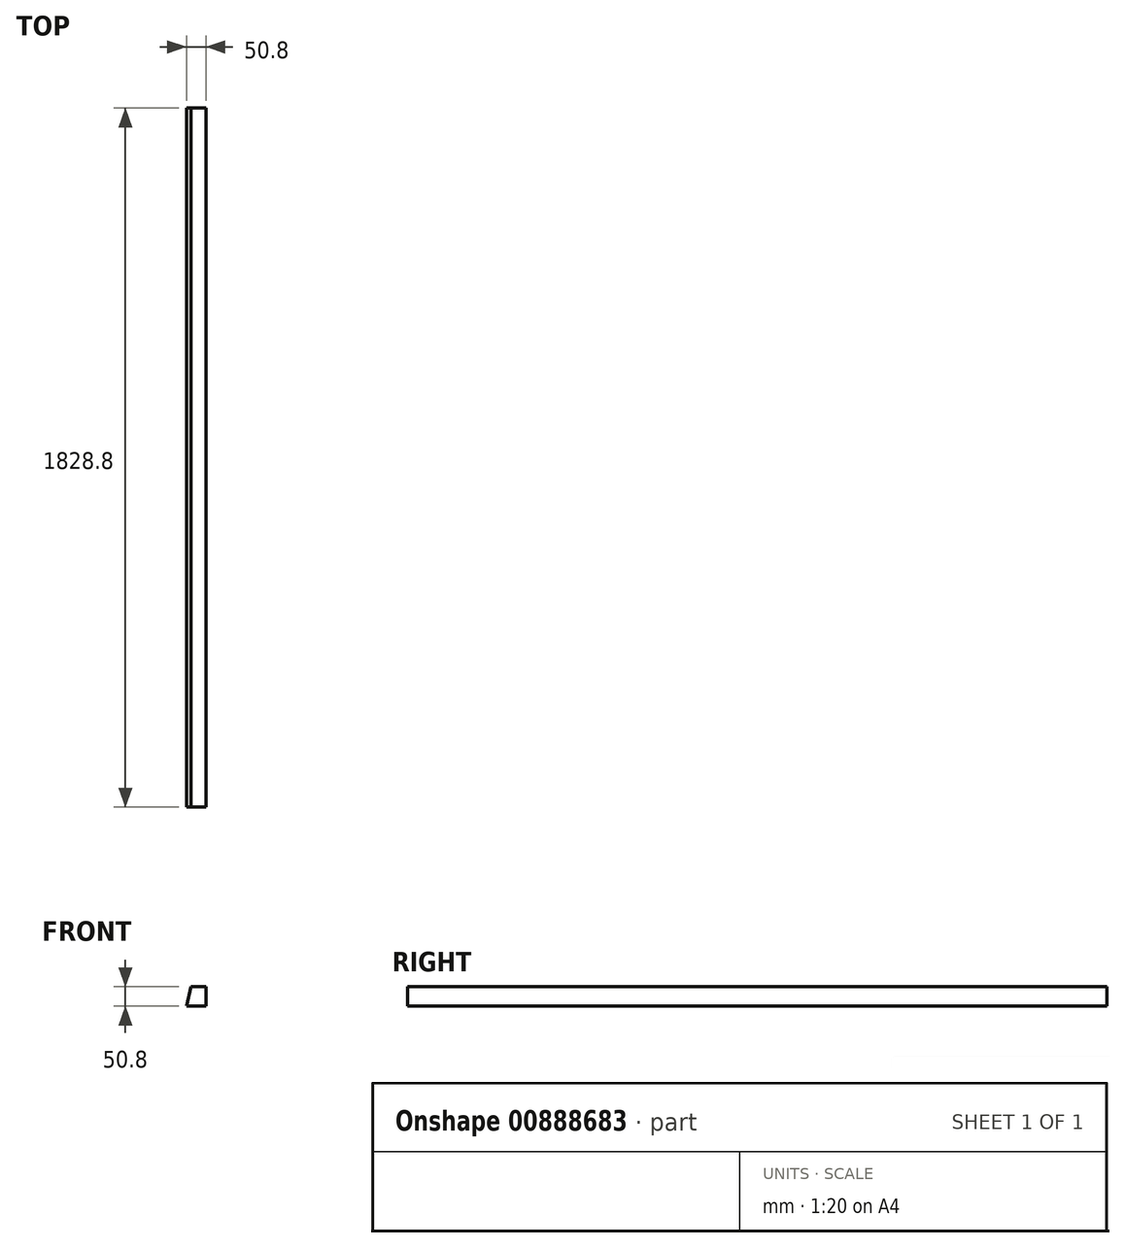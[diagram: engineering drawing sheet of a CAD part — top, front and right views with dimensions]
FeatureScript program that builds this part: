
annotation { "Feature Type Name" : "Feature", "Feature Type Description" : "" }
export const myFeature = defineFeature(function(context is Context, id is Id, definition is map)
    precondition{}
    {
        {
            var Q0;
            Q0=qCreatedBy(makeId("Right.planeOp"),FACE);
            var sketch = newSketch(context, id + "F0", { "sketchPlane" : qUnion([Q0])});
            skLineSegment(sketch, "E0.bottom", {"start": v(914.4, 25.4) * mm, "end": v(-914.4, 25.4) * mm});
            skLineSegment(sketch, "E0.top", {"start": v(914.4, -25.4) * mm, "end": v(-914.4, -25.4) * mm});
            skLineSegment(sketch, "E0.left", {"start": v(914.4, 25.4) * mm, "end": v(914.4, -25.4) * mm});
            skLineSegment(sketch, "E0.right", {"start": v(-914.4, 25.4) * mm, "end": v(-914.4, -25.4) * mm});
            skPoint(sketch, "E0.middle", {"position": v(0, 0) * mm});
            skSolve(sketch);
        }
        {
            var Q0;
            Q0=makeQuery(id+"F0.imprint","IMPRINT",FACE,{"disambiguationData":[TD([[makeQuery(id+"F0.imprint","IMPRINT",EDGE,{"derivedFrom":sQuery(id+"F0.wireOp",EDGE,"E0.bottom")}),1.0]])]});
            extrude(context, id + "F1", {"entities" : qUnion([Q0]), "depth" : 50.8 * mm, "offsetDistance" : 25.4 * mm});
        }
        {
            var Q0;
            Q0=makeQuery(id+"F1.opExtrude","SWEPT_FACE",FACE,{"disambiguationData":[OSD([sQuery(id+"F0.wireOp",EDGE,"E0.right")])]});
            var sketch = newSketch(context, id + "F2", { "sketchPlane" : qUnion([Q0])});
            skLineSegment(sketch, "E1", {"start": v(0, -25.4) * mm, "end": v(11.26, 25.4) * mm});
            skLineSegment(sketch, "E2", {"start": v(11.26, 25.4) * mm, "end": v(0, 25.4) * mm});
            skLineSegment(sketch, "E3", {"start": v(0, 25.4) * mm, "end": v(0, -25.4) * mm});
            skSolve(sketch);
        }
        {
            var Q0;
            Q0 = qSketchRegion(id + "F2", true);
            extrude(context, id + "F3", {"entities" : qUnion([Q0]), "operationType" : NewBodyOperationType.REMOVE, "endBound" : BoundingType.THROUGH_ALL, "oppositeDirection" : true, "depth" : 25.4 * mm, "offsetDistance" : 25.4 * mm});
        }
    });
